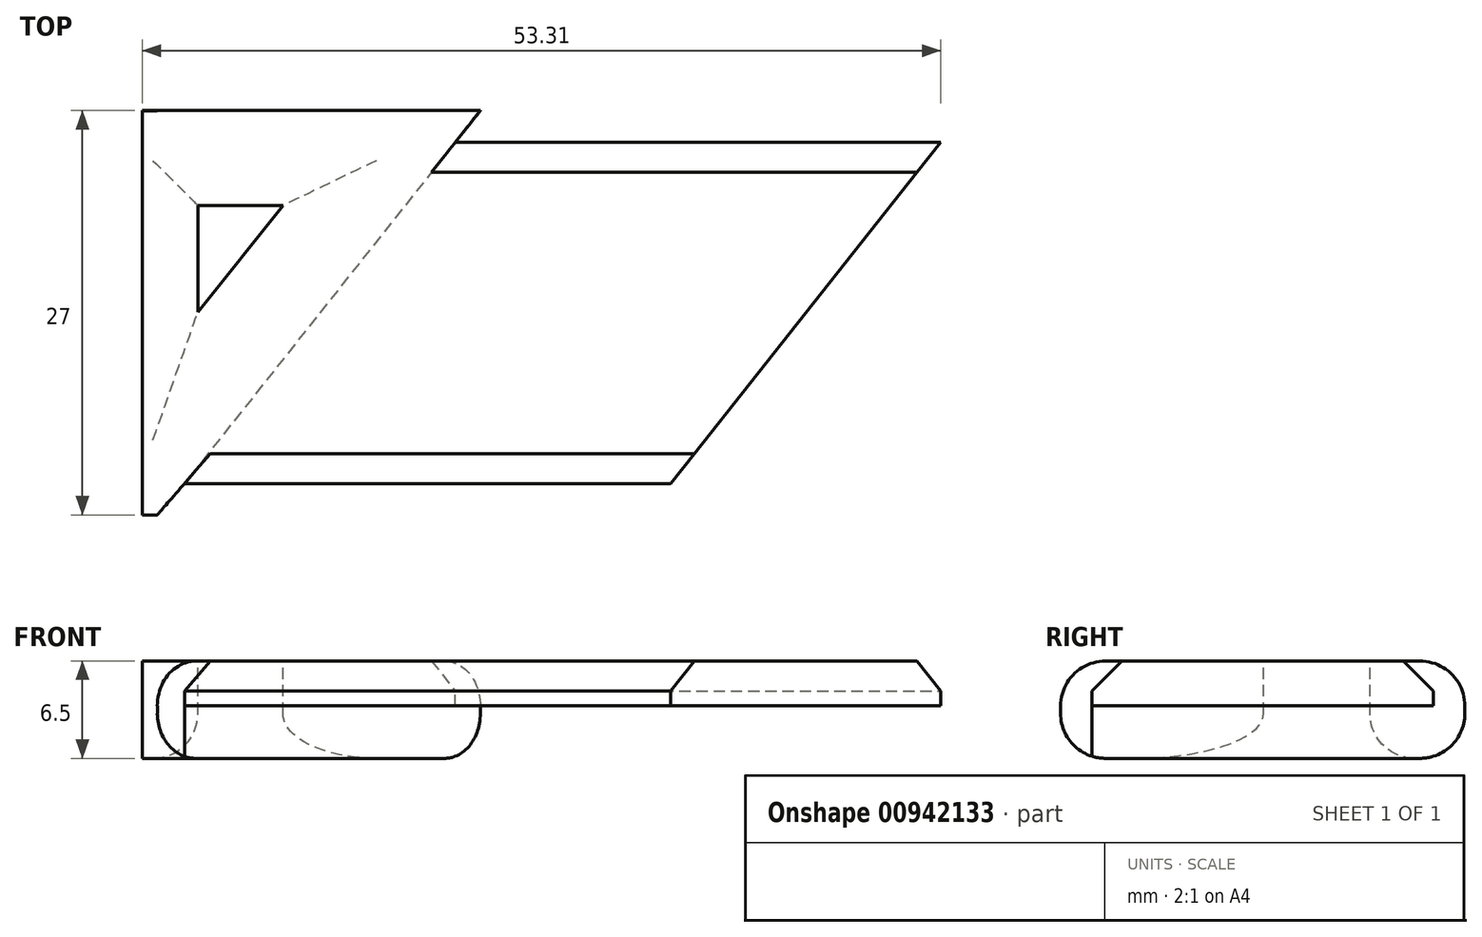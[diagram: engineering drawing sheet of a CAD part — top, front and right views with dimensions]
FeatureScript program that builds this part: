
annotation { "Feature Type Name" : "Feature", "Feature Type Description" : "" }
export const myFeature = defineFeature(function(context is Context, id is Id, definition is map)
    precondition{}
    {
        {
            var Q0;
            Q0=qCreatedBy(makeId("Top.planeOp"),FACE);
            var sketch = newSketch(context, id + "F0", { "sketchPlane" : qUnion([Q0])});
            skLineSegment(sketch, "E0", {"start": v(26.99, 13.44) * mm, "end": v(-5.51, 13.44) * mm, "construction": true});
            skLineSegment(sketch, "E1", {"start": v(-5.51, 13.44) * mm, "end": v(-8.7, 9.44) * mm, "construction": true});
            skLineSegment(sketch, "E2", {"start": v(-8.7, 9.44) * mm, "end": v(23.8, 9.44) * mm, "construction": true});
            skLineSegment(sketch, "E3", {"start": v(23.8, 9.44) * mm, "end": v(26.99, 13.44) * mm, "construction": true});
            skLineSegment(sketch, "E4", {"start": v(-27.08, -13.56) * mm, "end": v(5.43, -13.56) * mm, "construction": true});
            skLineSegment(sketch, "E5", {"start": v(5.43, -13.56) * mm, "end": v(8.61, -9.56) * mm, "construction": true});
            skLineSegment(sketch, "E6", {"start": v(8.61, -9.56) * mm, "end": v(-23.83, -9.56) * mm, "construction": true});
            skLineSegment(sketch, "E7", {"start": v(-23.83, -9.56) * mm, "end": v(-27.08, -13.56) * mm, "construction": true});
            skLineSegment(sketch, "E8", {"start": v(-7.18, 11.34) * mm, "end": v(25.23, 11.34) * mm, "construction": true});
            skLineSegment(sketch, "E9", {"start": v(-25.27, -11.46) * mm, "end": v(7.18, -11.46) * mm, "construction": true});
            skLineSegment(sketch, "E10", {"start": v(-27.08, -13.56) * mm, "end": v(-27.08, 13.44) * mm});
            skLineSegment(sketch, "E11", {"start": v(-27.08, 13.44) * mm, "end": v(-5.51, 13.44) * mm});
            skLineSegment(sketch, "E12", {"start": v(-7.18, 11.34) * mm, "end": v(25.23, 11.34) * mm});
            skLineSegment(sketch, "E13", {"start": v(7.18, -11.46) * mm, "end": v(25.23, 11.34) * mm});
            skLineSegment(sketch, "E14", {"start": v(7.18, -11.46) * mm, "end": v(-25.27, -11.46) * mm});
            skLineSegment(sketch, "E15", {"start": v(-7.18, 11.34) * mm, "end": v(-25.27, -11.46) * mm});
            skLineSegment(sketch, "E16", {"start": v(-5.51, 13.44) * mm, "end": v(-7.18, 11.34) * mm});
            skLineSegment(sketch, "E17", {"start": v(-27.08, -13.56) * mm, "end": v(-25.27, -11.46) * mm});
            skLineSegment(sketch, "E18", {"start": v(-27.08, 13.44) * mm, "end": v(-28.08, 13.44) * mm});
            skLineSegment(sketch, "E19", {"start": v(-28.08, 13.44) * mm, "end": v(-28.08, -13.56) * mm});
            skLineSegment(sketch, "E20", {"start": v(-28.08, -13.56) * mm, "end": v(-27.08, -13.56) * mm});
            skSolve(sketch);
        }
        {
            var Q0;
            Q0=qCreatedBy(makeId("Top.planeOp"),FACE);
            var sketch = newSketch(context, id + "F1", { "sketchPlane" : qUnion([Q0])});
            skLineSegment(sketch, "E21", {"start": v(-27.08, -13.56) * mm, "end": v(-27.08, 13.44) * mm});
            skLineSegment(sketch, "E22", {"start": v(-27.08, 13.44) * mm, "end": v(-5.51, 13.44) * mm});
            skLineSegment(sketch, "E23", {"start": v(-5.51, 13.44) * mm, "end": v(-27.08, -13.56) * mm});
            skLineSegment(sketch, "E24", {"start": v(-24.37, 7.1) * mm, "end": v(-18.7, 7.1) * mm});
            skLineSegment(sketch, "E25", {"start": v(-18.7, 7.1) * mm, "end": v(-24.37, 0) * mm});
            skLineSegment(sketch, "E26", {"start": v(-24.37, 0) * mm, "end": v(-24.37, 7.1) * mm});
            skLineSegment(sketch, "E27", {"start": v(-27.08, 13.44) * mm, "end": v(-28.08, 13.44) * mm});
            skLineSegment(sketch, "E28", {"start": v(-28.08, 13.44) * mm, "end": v(-28.08, -13.56) * mm});
            skLineSegment(sketch, "E29", {"start": v(-28.08, -13.56) * mm, "end": v(-27.08, -13.56) * mm});
            skSolve(sketch);
        }
        {
            var Q0;
            Q0=makeQuery(id+"F0.imprint","IMPRINT",FACE,{"disambiguationData":[TD([[makeQuery(id+"F0.imprint","IMPRINT",EDGE,{"derivedFrom":sQuery(id+"F0.wireOp",EDGE,"E10")}),-1.0]])]});
            var Q1;
            Q1=makeQuery(id+"F0.imprint","IMPRINT",FACE,{"disambiguationData":[TD([[makeQuery(id+"F0.imprint","IMPRINT",EDGE,{"derivedFrom":sQuery(id+"F0.wireOp",EDGE,"E12")}),-1.0]])]});
            var Q2;
            Q2=makeQuery(id+"F0.imprint","IMPRINT",FACE,{"disambiguationData":[TD([[makeQuery(id+"F0.imprint","IMPRINT",EDGE,{"derivedFrom":sQuery(id+"F0.wireOp",EDGE,"E10")}),1.0]])]});
            extrude(context, id + "F2", {"entities" : qUnion([Q0, Q1, Q2]), "oppositeDirection" : true, "depth" : 3 * mm, "offsetDistance" : 25 * mm});
        }
        {
            var Q0;
            Q0=makeQuery(id+"F0.imprint","IMPRINT",FACE,{"disambiguationData":[TD([[makeQuery(id+"F0.imprint","IMPRINT",EDGE,{"derivedFrom":sQuery(id+"F0.wireOp",EDGE,"E10")}),-1.0]])]});
            var Q1;
            Q1=qSketchRegion(id+"F1",true);
            extrude(context, id + "F3", {"entities" : qUnion([Q0, Q1]), "operationType" : NewBodyOperationType.ADD, "oppositeDirection" : true, "depth" : 6.5 * mm, "offsetDistance" : 25 * mm});
        }
        {
            var Q0;
            Q0=makeQuery(id+"F2.opExtrude","CAP_EDGE",EDGE,{"disambiguationData":[OSD([sQuery(id+"F0.wireOp",EDGE,"E12")])],"isStart":true});
            var Q1;
            Q1=makeQuery(id+"F2.opExtrude","CAP_EDGE",EDGE,{"disambiguationData":[OSD([sQuery(id+"F0.wireOp",EDGE,"E14")])],"isStart":true});
            chamfer(context, id + "F4", {"entities" : qUnion([Q0, Q1]), "width" : 2 * mm, "tangentPropagation" : true});
        }
        {
            var Q0;
            Q0=makeQuery(id+"F2.opExtrude","CAP_EDGE",EDGE,{"disambiguationData":[OSD([sQuery(id+"F0.wireOp",EDGE,"E11")])],"isStart":true});
            var Q1;
            Q1=makeQuery(id+"F3.opExtrude","CAP_EDGE",EDGE,{"disambiguationData":[OSD([sQuery(id+"F0.wireOp",EDGE,"E11")])],"isStart":false});
            var Q2;
            Q2=makeQuery(id+"F2.opExtrude","CAP_EDGE",EDGE,{"disambiguationData":[OSD([sQuery(id+"F0.wireOp",EDGE,"7gGAPOjL-t7sV-ewJa-ArCT-nc4j6WmRso13")])],"isStart":true});
            var Q3;
            Q3=makeQuery(id+"F2.opExtrude","CAP_EDGE",EDGE,{"disambiguationData":[OSD([sQuery(id+"F0.wireOp",EDGE,"yde29xXl-ICFn-0QiE-HzA1-EqmZUxvuQBXi")])],"isStart":true});
            var Q4;
            Q4=makeQuery(id+"F2.opExtrude","CAP_EDGE",EDGE,{"disambiguationData":[OSD([sQuery(id+"F0.wireOp",EDGE,"CeoQsM6z-U6Wm-WrTS-g2a8-tBGnORVz6SGF")])],"isStart":true});
            var Q5;
            Q5=makeQuery(id+"F3.opExtrude","CAP_EDGE",EDGE,{"disambiguationData":[OSD([sQuery(id+"F0.wireOp",EDGE,"7gGAPOjL-t7sV-ewJa-ArCT-nc4j6WmRso13")])],"isStart":false});
            var Q6;
            Q6=makeQuery(id+"F3.opExtrude","CAP_EDGE",EDGE,{"disambiguationData":[OSD([sQuery(id+"F0.wireOp",EDGE,"CeoQsM6z-U6Wm-WrTS-g2a8-tBGnORVz6SGF")])],"isStart":false});
            var Q7;
            Q7=makeQuery(id+"F3.opExtrude","CAP_EDGE",EDGE,{"disambiguationData":[OSD([sQuery(id+"F0.wireOp",EDGE,"yde29xXl-ICFn-0QiE-HzA1-EqmZUxvuQBXi")])],"isStart":false});
            var Q8;
            Q8=makeQuery(id+"F3.opExtrude","CAP_EDGE",EDGE,{"disambiguationData":[OSD([sQuery(id+"F1.wireOp",EDGE,"E29")])],"isStart":false});
            var Q9;
            Q9=makeQuery(id+"F2.opExtrude","CAP_EDGE",EDGE,{"disambiguationData":[OSD([sQuery(id+"F0.wireOp",EDGE,"E20")])],"isStart":true});
            fillet(context, id + "F5", {"entities" : qUnion([Q0, Q1, Q2, Q3, Q4, Q5, Q6, Q7, Q8, Q9]), "radius" : 3 * mm, "tangentPropagation" : true, "allowEdgeOverflow" : false});
        }
        {
            var Q0;
            Q0=makeQuery(id+"F1.imprint","IMPRINT",FACE,{"disambiguationData":[TD([[makeQuery(id+"F1.imprint","IMPRINT",EDGE,{"derivedFrom":sQuery(id+"F1.wireOp",EDGE,"E24")}),-1.0]])]});
            extrude(context, id + "F6", {"entities" : qUnion([Q0]), "operationType" : NewBodyOperationType.REMOVE, "endBound" : BoundingType.THROUGH_ALL, "oppositeDirection" : true, "depth" : 25 * mm, "offsetDistance" : 25 * mm});
        }
        {
            var Q0;
            Q0=makeQuery(id+"F6.boolean.opBoolean","COPY",EDGE,{"derivedFrom":makeQuery(id+"F6.opExtrude","CAP_EDGE",EDGE,{"disambiguationData":[OSD([sQuery(id+"F1.wireOp",EDGE,"E25")])],"isStart":true})});
            var Q1;
            Q1=makeQuery(id+"F6.boolean.opBoolean","COPY",EDGE,{"derivedFrom":makeQuery(id+"F6.opExtrude","CAP_EDGE",EDGE,{"disambiguationData":[OSD([sQuery(id+"F1.wireOp",EDGE,"E24")])],"isStart":true})});
            var Q2;
            Q2=makeQuery(id+"F6.boolean.opBoolean","COPY",EDGE,{"derivedFrom":makeQuery(id+"F6.opExtrude","CAP_EDGE",EDGE,{"disambiguationData":[OSD([sQuery(id+"F1.wireOp",EDGE,"E26")])],"isStart":true})});
            var Q3;
            Q3=makeQuery(id+"F6.boolean.opBoolean","INTERSECT",EDGE,{"derivedFrom":[makeQuery(id+"F3.opExtrude","CAP_FACE",FACE,{"disambiguationData":[OSD([sQuery(id+"F0.wireOp",EDGE,"E10"),sQuery(id+"F0.wireOp",EDGE,"E11"),sQuery(id+"F0.wireOp",EDGE,"E15"),sQuery(id+"F0.wireOp",EDGE,"E16"),sQuery(id+"F0.wireOp",EDGE,"E17")])],"isStart":false}),makeQuery(id+"F6.opExtrude","SWEPT_FACE",FACE,{"disambiguationData":[OSD([sQuery(id+"F1.wireOp",EDGE,"E24")])]})]});
            var Q4;
            Q4=makeQuery(id+"F6.boolean.opBoolean","INTERSECT",EDGE,{"derivedFrom":[makeQuery(id+"F3.opExtrude","CAP_FACE",FACE,{"disambiguationData":[OSD([sQuery(id+"F0.wireOp",EDGE,"E10"),sQuery(id+"F0.wireOp",EDGE,"E11"),sQuery(id+"F0.wireOp",EDGE,"E15"),sQuery(id+"F0.wireOp",EDGE,"E16"),sQuery(id+"F0.wireOp",EDGE,"E17")])],"isStart":false}),makeQuery(id+"F6.opExtrude","SWEPT_FACE",FACE,{"disambiguationData":[OSD([sQuery(id+"F1.wireOp",EDGE,"E26")])]})]});
            var Q5;
            Q5=makeQuery(id+"F6.boolean.opBoolean","INTERSECT",EDGE,{"derivedFrom":[makeQuery(id+"F3.opExtrude","CAP_FACE",FACE,{"disambiguationData":[OSD([sQuery(id+"F0.wireOp",EDGE,"E10"),sQuery(id+"F0.wireOp",EDGE,"E11"),sQuery(id+"F0.wireOp",EDGE,"E15"),sQuery(id+"F0.wireOp",EDGE,"E16"),sQuery(id+"F0.wireOp",EDGE,"E17")])],"isStart":false}),makeQuery(id+"F6.opExtrude","SWEPT_FACE",FACE,{"disambiguationData":[OSD([sQuery(id+"F1.wireOp",EDGE,"E25")])]})]});
            fillet(context, id + "F7", {"entities" : qUnion([Q0, Q1, Q2, Q3, Q4, Q5]), "radius" : 3 * mm, "tangentPropagation" : true, "allowEdgeOverflow" : false});
        }
    });
